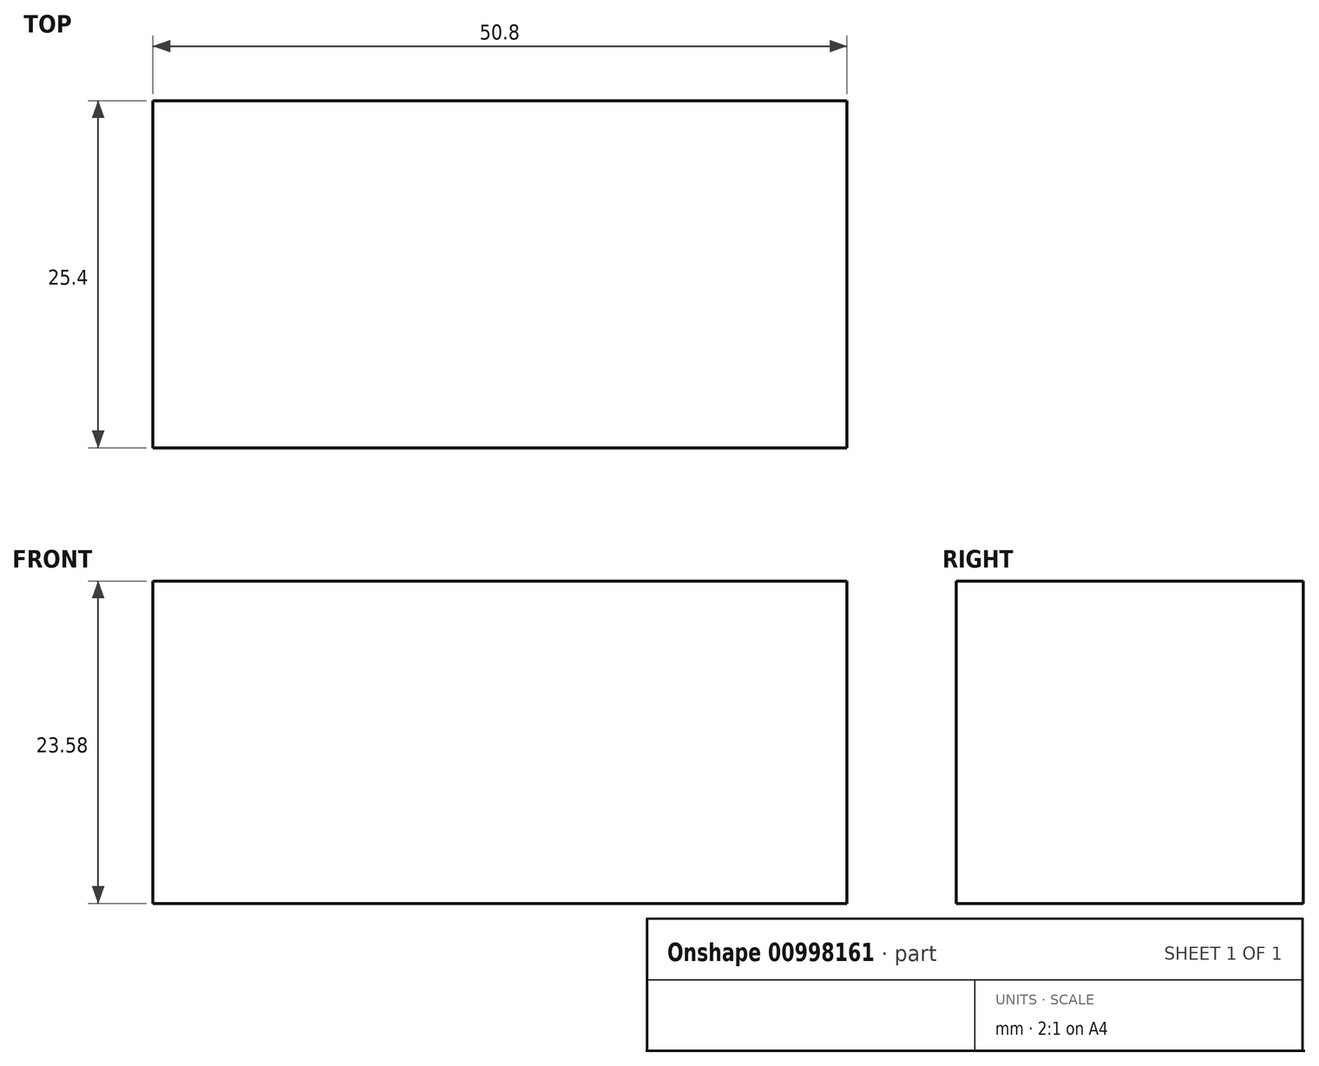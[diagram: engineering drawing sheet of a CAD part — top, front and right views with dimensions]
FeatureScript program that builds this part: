
annotation { "Feature Type Name" : "Feature", "Feature Type Description" : "" }
export const myFeature = defineFeature(function(context is Context, id is Id, definition is map)
    precondition{}
    {
        {
            var Q0;
            Q0=qCreatedBy(makeId("Front.planeOp"),FACE);
            var sketch = newSketch(context, id + "F0", { "sketchPlane" : qUnion([Q0])});
            skLineSegment(sketch, "E0.bottom", {"start": v(0, 7.35) * mm, "end": v(50.8, 7.35) * mm});
            skLineSegment(sketch, "E0.top", {"start": v(0, -16.23) * mm, "end": v(50.8, -16.23) * mm});
            skLineSegment(sketch, "E0.left", {"start": v(0, 7.35) * mm, "end": v(0, -16.23) * mm});
            skLineSegment(sketch, "E0.right", {"start": v(50.8, 7.35) * mm, "end": v(50.8, -16.23) * mm});
            skSolve(sketch);
        }
        {
            var Q0;
            Q0=makeQuery(id+"F0.imprint","IMPRINT",FACE,{"disambiguationData":[TD([[makeQuery(id+"F0.imprint","IMPRINT",EDGE,{"derivedFrom":sQuery(id+"F0.wireOp",EDGE,"E0.bottom")}),-1.0]])]});
            extrude(context, id + "F1", {"entities" : qUnion([Q0]), "depth" : 25.4 * mm, "offsetDistance" : 25.4 * mm});
        }
    });
